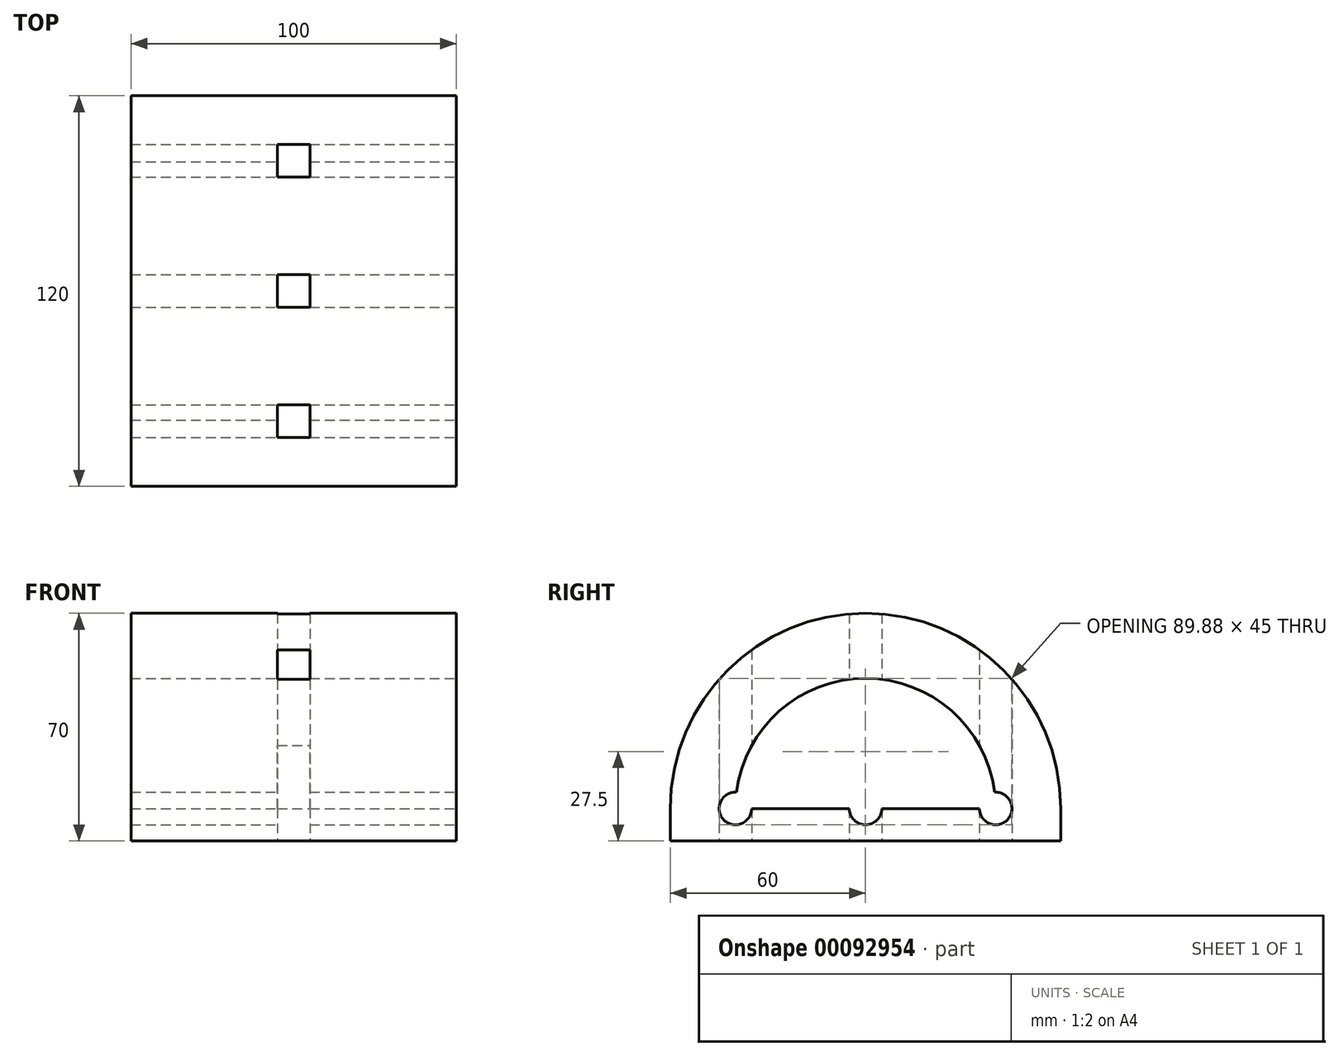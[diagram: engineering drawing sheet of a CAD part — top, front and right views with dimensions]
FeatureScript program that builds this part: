
annotation { "Feature Type Name" : "Feature", "Feature Type Description" : "" }
export const myFeature = defineFeature(function(context is Context, id is Id, definition is map)
    precondition{}
    {
        {
            var Q0;
            Q0=qCreatedBy(makeId("Right.planeOp"),FACE);
            var sketch = newSketch(context, id + "F0", { "sketchPlane" : qUnion([Q0])});
            skLineSegment(sketch, "E0.bottom", {"start": v(60, -5) * mm, "end": v(-60, -5) * mm});
            skLineSegment(sketch, "E0.top", {"start": v(60, 5) * mm, "end": v(-60, 5) * mm});
            skLineSegment(sketch, "E0.left", {"start": v(60, -5) * mm, "end": v(60, 5) * mm});
            skLineSegment(sketch, "E0.right", {"start": v(-60, -5) * mm, "end": v(-60, 5) * mm});
            skPoint(sketch, "E0.middle", {"position": v(0, 0) * mm});
            skArc(sketch, "E1", {"start": v(60, 5) * mm, "mid": v(0, 65) * mm, "end": v(-60, 5) * mm});
            skSolve(sketch);
        }
        {
            var Q0;
            Q0 = qSketchRegion(id + "F0", true);
            extrude(context, id + "F1", {"entities" : qUnion([Q0]), "depth" : 100 * mm});
        }
        {
            var Q0;
            Q0=makeQuery(id+"F1.opExtrude","CAP_FACE",FACE,{"disambiguationData":[OSD([sQuery(id+"F0.wireOp",EDGE,"E0.bottom"),sQuery(id+"F0.wireOp",EDGE,"E0.left"),sQuery(id+"F0.wireOp",EDGE,"E0.right"),sQuery(id+"F0.wireOp",EDGE,"E1")])],"isStart":false});
            var sketch = newSketch(context, id + "F2", { "sketchPlane" : qUnion([Q0])});
            skCircle(sketch, "E2", {"center": v(0, 5) * mm, "radius": 5 * mm});
            skCircle(sketch, "E3", {"center": v(40, 5) * mm, "radius": 5 * mm});
            skCircle(sketch, "E4", {"center": v(-40, 5) * mm, "radius": 5 * mm});
            skLineSegment(sketch, "E5", {"start": v(0, 0) * mm, "end": v(0, -5) * mm, "construction": true});
            skPoint(sketch, "E6", {"position": v(20, 5) * mm});
            skPoint(sketch, "E7.centerSnap0", {"position": v(-20, 5) * mm});
            skArc(sketch, "E8", {"start": v(40, 5) * mm, "mid": v(0, 45) * mm, "end": v(-40, 5) * mm});
            skLineSegment(sketch, "E9", {"start": v(-40, 5) * mm, "end": v(40, 5) * mm});
            skSolve(sketch);
        }
        {
            var Q0;
            Q0 = qSketchRegion(id + "F2", true);
            extrude(context, id + "F3", {"entities" : qUnion([Q0]), "operationType" : NewBodyOperationType.REMOVE, "endBound" : BoundingType.THROUGH_ALL, "oppositeDirection" : true, "depth" : 25 * mm});
        }
        {
            var Q0;
            Q0=makeQuery(id+"F1.opExtrude","SWEPT_FACE",FACE,{"disambiguationData":[OSD([sQuery(id+"F0.wireOp",EDGE,"E0.bottom")])]});
            var sketch = newSketch(context, id + "F4", { "sketchPlane" : qUnion([Q0])});
            skLineSegment(sketch, "E10.bottom", {"start": v(45, -5) * mm, "end": v(55, -5) * mm});
            skLineSegment(sketch, "E10.top", {"start": v(45, 5) * mm, "end": v(55, 5) * mm});
            skLineSegment(sketch, "E10.left", {"start": v(45, -5) * mm, "end": v(45, 5) * mm});
            skLineSegment(sketch, "E10.right", {"start": v(55, -5) * mm, "end": v(55, 5) * mm});
            skPoint(sketch, "E10.middle", {"position": v(50, 0) * mm});
            skPoint(sketch, "E10.middle.positionSnap0", {"position": v(50, -60) * mm});
            skPoint(sketch, "E10.middle.positionSnap1", {"position": v(100, 0) * mm});
            skPoint(sketch, "E10.centerSnap0", {"position": v(50, -60) * mm});
            skPoint(sketch, "E10.centerSnap1", {"position": v(100, 0) * mm});
            skLineSegment(sketch, "E11.bottom", {"start": v(55, -45) * mm, "end": v(45, -45) * mm});
            skLineSegment(sketch, "E11.top", {"start": v(55, -35) * mm, "end": v(45, -35) * mm});
            skLineSegment(sketch, "E11.left", {"start": v(55, -45) * mm, "end": v(55, -35) * mm});
            skLineSegment(sketch, "E11.right", {"start": v(45, -45) * mm, "end": v(45, -35) * mm});
            skPoint(sketch, "E11.middle", {"position": v(50, -40) * mm});
            skLineSegment(sketch, "E12.bottom", {"start": v(55, 35) * mm, "end": v(45, 35) * mm});
            skLineSegment(sketch, "E12.top", {"start": v(55, 45) * mm, "end": v(45, 45) * mm});
            skLineSegment(sketch, "E12.left", {"start": v(55, 35) * mm, "end": v(55, 45) * mm});
            skLineSegment(sketch, "E12.right", {"start": v(45, 35) * mm, "end": v(45, 45) * mm});
            skPoint(sketch, "E12.middle", {"position": v(50, 40) * mm});
            skSolve(sketch);
        }
        {
            var Q0;
            Q0 = qSketchRegion(id + "F4", true);
            extrude(context, id + "F5", {"entities" : qUnion([Q0]), "operationType" : NewBodyOperationType.REMOVE, "endBound" : BoundingType.THROUGH_ALL, "oppositeDirection" : true, "depth" : 25 * mm});
        }
    });
